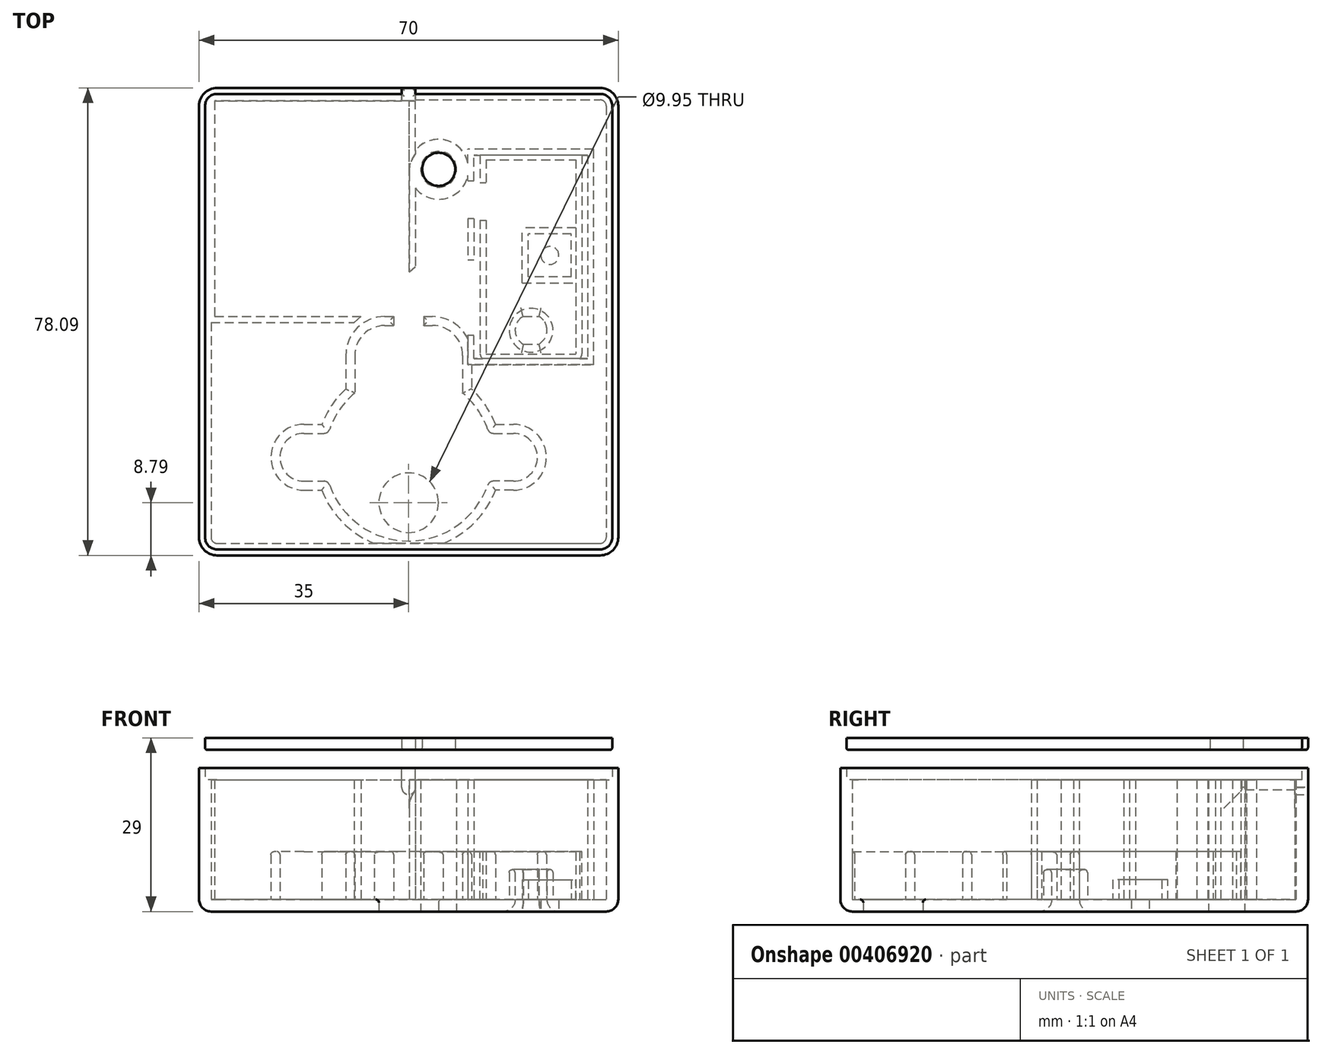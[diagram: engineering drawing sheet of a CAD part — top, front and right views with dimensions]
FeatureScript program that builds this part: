
annotation { "Feature Type Name" : "Feature", "Feature Type Description" : "" }
export const myFeature = defineFeature(function(context is Context, id is Id, definition is map)
    precondition{}
    {
        {
            var Q0;
            Q0=qCreatedBy(makeId("Top.planeOp"),FACE);
            var sketch = newSketch(context, id + "F0", { "sketchPlane" : qUnion([Q0])});
            skCircle(sketch, "E0", {"center": v(0, 0) * mm, "radius": 4.97 * mm});
            skArc(sketch, "E1", {"start": v(-13.2, 2.93) * mm, "mid": v(0, -6.4) * mm, "end": v(13.2, 2.93) * mm});
            skArc(sketch, "E2.trimOffspring", {"start": v(13.2, 12.27) * mm, "mid": v(11.5, 15.58) * mm, "end": v(9, 18.32) * mm});
            skLineSegment(sketch, "E3", {"start": v(-9, 24.6) * mm, "end": v(-9, 18.32) * mm});
            skLineSegment(sketch, "E4.MirrorCS", {"start": v(9, 24.6) * mm, "end": v(9, 18.32) * mm});
            skLineSegment(sketch, "E5", {"start": v(-4, 29.6) * mm, "end": v(4, 29.6) * mm});
            skArc(sketch, "E6.filletArc", {"start": v(-4, 29.6) * mm, "mid": v(-7.54, 28.14) * mm, "end": v(-9, 24.6) * mm});
            skArc(sketch, "E7.filletArc", {"start": v(9, 24.6) * mm, "mid": v(7.54, 28.14) * mm, "end": v(4, 29.6) * mm});
            skArc(sketch, "E8.trimOffspring", {"start": v(-9, 18.32) * mm, "mid": v(-11.5, 15.58) * mm, "end": v(-13.2, 12.27) * mm});
            skLineSegment(sketch, "E9", {"start": v(-17.5, 11.6) * mm, "end": v(-14.14, 11.6) * mm});
            skLineSegment(sketch, "E10", {"start": v(-17.5, 3.6) * mm, "end": v(-14.14, 3.6) * mm});
            skLineSegment(sketch, "E11", {"start": v(21.5, 7.6) * mm, "end": v(21.5, 7.6) * mm});
            skArc(sketch, "E12.filletArc", {"start": v(21.5, 7.6) * mm, "mid": v(20.33, 10.43) * mm, "end": v(17.5, 11.6) * mm});
            skArc(sketch, "E13.filletArc", {"start": v(17.5, 3.6) * mm, "mid": v(20.33, 4.77) * mm, "end": v(21.5, 7.6) * mm});
            skArc(sketch, "E14.MirrorCS", {"start": v(-21.5, 7.6) * mm, "mid": v(-20.33, 10.43) * mm, "end": v(-17.5, 11.6) * mm});
            skLineSegment(sketch, "E15.MirrorCS", {"start": v(-21.5, 7.6) * mm, "end": v(-21.5, 7.6) * mm});
            skArc(sketch, "E16.MirrorCS", {"start": v(-17.5, 3.6) * mm, "mid": v(-20.33, 4.77) * mm, "end": v(-21.5, 7.6) * mm});
            skLineSegment(sketch, "E17.trimOffspring", {"start": v(14.14, 11.6) * mm, "end": v(17.5, 11.6) * mm});
            skArc(sketch, "E18.filletArc", {"start": v(-14.14, 11.6) * mm, "mid": v(-13.56, 11.78) * mm, "end": v(-13.2, 12.27) * mm});
            skArc(sketch, "E19.filletArc", {"start": v(-13.2, 2.93) * mm, "mid": v(-13.56, 3.42) * mm, "end": v(-14.14, 3.6) * mm});
            skLineSegment(sketch, "E20.MirrorCS", {"start": v(17.5, 3.6) * mm, "end": v(14.14, 3.6) * mm});
            skArc(sketch, "E21.MirrorCS", {"start": v(13.2, 2.93) * mm, "mid": v(13.56, 3.42) * mm, "end": v(14.14, 3.6) * mm});
            skArc(sketch, "E22.0", {"start": v(-4, 31.1) * mm, "mid": v(-8.6, 29.2) * mm, "end": v(-10.5, 24.6) * mm});
            skLineSegment(sketch, "E22.1", {"start": v(-10.5, 24.6) * mm, "end": v(-10.5, 19) * mm});
            skArc(sketch, "E22.2", {"start": v(-10.5, 19) * mm, "mid": v(-12.84, 16.28) * mm, "end": v(-14.5, 13.1) * mm});
            skLineSegment(sketch, "E22.3", {"start": v(-17.5, 13.1) * mm, "end": v(-14.5, 13.1) * mm});
            skArc(sketch, "E22.4", {"start": v(-23, 7.6) * mm, "mid": v(-21.39, 11.49) * mm, "end": v(-17.5, 13.1) * mm});
            skLineSegment(sketch, "E22.5", {"start": v(14.5, 13.1) * mm, "end": v(17.5, 13.1) * mm});
            skArc(sketch, "E22.6", {"start": v(14.5, 13.1) * mm, "mid": v(12.84, 16.28) * mm, "end": v(10.5, 19) * mm});
            skLineSegment(sketch, "E22.7", {"start": v(10.5, 24.6) * mm, "end": v(10.5, 19) * mm});
            skArc(sketch, "E22.8", {"start": v(10.5, 24.6) * mm, "mid": v(8.6, 29.2) * mm, "end": v(4, 31.1) * mm});
            skArc(sketch, "E22.9", {"start": v(23, 7.6) * mm, "mid": v(21.39, 11.49) * mm, "end": v(17.5, 13.1) * mm});
            skArc(sketch, "E22.10", {"start": v(17.5, 2.1) * mm, "mid": v(21.39, 3.71) * mm, "end": v(23, 7.6) * mm});
            skLineSegment(sketch, "E22.11", {"start": v(17.5, 2.1) * mm, "end": v(14.5, 2.1) * mm});
            skArc(sketch, "E22.12", {"start": v(-14.5, 2.1) * mm, "mid": v(0, -7.9) * mm, "end": v(14.5, 2.1) * mm});
            skLineSegment(sketch, "E22.13", {"start": v(-17.5, 2.1) * mm, "end": v(-14.5, 2.1) * mm});
            skLineSegment(sketch, "E22.14", {"start": v(-4, 31.1) * mm, "end": v(4, 31.1) * mm});
            skArc(sketch, "E22.15", {"start": v(-17.5, 2.1) * mm, "mid": v(-21.39, 3.71) * mm, "end": v(-23, 7.6) * mm});
            skPoint(sketch, "E23.visualSharp", {"position": v(13.42, 11.6) * mm});
            skArc(sketch, "E23.filletArc", {"start": v(13.2, 12.27) * mm, "mid": v(13.56, 11.78) * mm, "end": v(14.14, 11.6) * mm});
            skLineSegment(sketch, "E24", {"start": v(-2.49, 31.1) * mm, "end": v(-2.49, 29.6) * mm});
            skLineSegment(sketch, "E25.MirrorCS", {"start": v(2.49, 31.1) * mm, "end": v(2.49, 29.6) * mm});
            skSolve(sketch);
        }
        {
            var Q0;
            Q0=makeQuery(id+"F0.imprint","IMPRINT",FACE,{"disambiguationData":[TD([[makeQuery(id+"F0.imprint","IMPRINT",EDGE,{"derivedFrom":sQuery(id+"F0.wireOp",EDGE,"E0")}),-1.0]])]});
            extrude(context, id + "F1", {"entities" : qUnion([Q0]), "depth" : 1.5 * mm, "offsetDistance" : 25 * mm});
        }
        {
            var Q0;
            Q0=makeQuery(id+"F0.imprint","IMPRINT",FACE,{"disambiguationData":[TD([[makeQuery(id+"F0.imprint","IMPRINT",EDGE,{"derivedFrom":sQuery(id+"F0.wireOp",EDGE,"E1")}),-1.0]])]});
            extrude(context, id + "F2", {"entities" : qUnion([Q0]), "operationType" : NewBodyOperationType.ADD, "depth" : 10 * mm});
        }
        {
            var Q0;
            Q0=qCreatedBy(makeId("Top.planeOp"),FACE);
            var sketch = newSketch(context, id + "F3", { "sketchPlane" : qUnion([Q0])});
            skLineSegment(sketch, "E26.bottom", {"start": v(-32, 67.3) * mm, "end": v(32, 67.3) * mm});
            skLineSegment(sketch, "E26.top", {"start": v(-32, -6.79) * mm, "end": v(32, -6.79) * mm});
            skLineSegment(sketch, "E26.left", {"start": v(-33, 66.3) * mm, "end": v(-33, -5.79) * mm});
            skLineSegment(sketch, "E26.right", {"start": v(33, 66.3) * mm, "end": v(33, -5.79) * mm});
            skPoint(sketch, "E27.visualSharp", {"position": v(-33, 67.3) * mm});
            skArc(sketch, "E27.filletArc", {"start": v(-32, 67.3) * mm, "mid": v(-32.7, 67) * mm, "end": v(-33, 66.3) * mm});
            skPoint(sketch, "E28.visualSharp", {"position": v(33, 67.3) * mm});
            skArc(sketch, "E28.filletArc", {"start": v(33, 66.3) * mm, "mid": v(32.7, 67) * mm, "end": v(32, 67.3) * mm});
            skPoint(sketch, "E29.visualSharp", {"position": v(-33, -6.79) * mm});
            skArc(sketch, "E29.filletArc", {"start": v(-33, -5.79) * mm, "mid": v(-32.7, -6.5) * mm, "end": v(-32, -6.79) * mm});
            skPoint(sketch, "E30.visualSharp", {"position": v(33, -6.79) * mm});
            skArc(sketch, "E30.filletArc", {"start": v(32, -6.79) * mm, "mid": v(32.7, -6.5) * mm, "end": v(33, -5.79) * mm});
            skArc(sketch, "E31.0", {"start": v(34, 66.3) * mm, "mid": v(33.41, 67.71) * mm, "end": v(32, 68.3) * mm});
            skLineSegment(sketch, "E31.1", {"start": v(-32, 68.3) * mm, "end": v(32, 68.3) * mm});
            skLineSegment(sketch, "E31.2", {"start": v(34, 66.3) * mm, "end": v(34, -5.79) * mm});
            skArc(sketch, "E31.3", {"start": v(-32, 68.3) * mm, "mid": v(-33.41, 67.71) * mm, "end": v(-34, 66.3) * mm});
            skArc(sketch, "E31.4", {"start": v(32, -7.79) * mm, "mid": v(33.41, -7.2) * mm, "end": v(34, -5.79) * mm});
            skLineSegment(sketch, "E31.5", {"start": v(-32, -7.79) * mm, "end": v(32, -7.79) * mm});
            skArc(sketch, "E31.6", {"start": v(-34, -5.79) * mm, "mid": v(-33.41, -7.2) * mm, "end": v(-32, -7.79) * mm});
            skLineSegment(sketch, "E31.7", {"start": v(-34, 66.3) * mm, "end": v(-34, -5.79) * mm});
            skArc(sketch, "E32.0", {"start": v(35, 66.3) * mm, "mid": v(34.12, 68.42) * mm, "end": v(32, 69.3) * mm});
            skLineSegment(sketch, "E32.1", {"start": v(-32, 69.3) * mm, "end": v(32, 69.3) * mm});
            skLineSegment(sketch, "E32.2", {"start": v(35, 66.3) * mm, "end": v(35, -5.79) * mm});
            skArc(sketch, "E32.3", {"start": v(-32, 69.3) * mm, "mid": v(-34.12, 68.42) * mm, "end": v(-35, 66.3) * mm});
            skArc(sketch, "E32.4", {"start": v(32, -8.79) * mm, "mid": v(34.12, -7.9) * mm, "end": v(35, -5.79) * mm});
            skLineSegment(sketch, "E32.5", {"start": v(-32, -8.79) * mm, "end": v(32, -8.79) * mm});
            skArc(sketch, "E32.6", {"start": v(-35, -5.79) * mm, "mid": v(-34.12, -7.9) * mm, "end": v(-32, -8.79) * mm});
            skLineSegment(sketch, "E32.7", {"start": v(-35, 66.3) * mm, "end": v(-35, -5.79) * mm});
            skSolve(sketch);
        }
        {
            var Q0;
            Q0=makeQuery(id+"F3.imprint","IMPRINT",FACE,{"disambiguationData":[TD([[makeQuery(id+"F3.imprint","IMPRINT",EDGE,{"derivedFrom":sQuery(id+"F3.wireOp",EDGE,"E26.bottom")}),-1.0]])]});
            extrude(context, id + "F4", {"entities" : qUnion([Q0]), "operationType" : NewBodyOperationType.ADD, "depth" : 2 * mm, "offsetDistance" : 25 * mm});
        }
        {
            var Q0;
            Q0=makeQuery(id+"F0.imprint","IMPRINT",FACE,{"disambiguationData":[TD([[makeQuery(id+"F0.imprint","IMPRINT",EDGE,{"derivedFrom":sQuery(id+"F0.wireOp",EDGE,"E0")}),1.0]])]});
            extrude(context, id + "F5", {"entities" : qUnion([Q0]), "operationType" : NewBodyOperationType.REMOVE, "depth" : 25 * mm, "offsetDistance" : 25 * mm});
        }
        {
            var Q0;
            {var subQ0=sQuery(id+"F3.wireOp",EDGE,"E26.bottom");var subQ1=sQuery(id+"F3.wireOp",EDGE,"E26.top");var subQ2=sQuery(id+"F3.wireOp",EDGE,"E26.left");var subQ3=sQuery(id+"F3.wireOp",EDGE,"E26.right");Q0=makeQuery(id+"F4.boolean.opBoolean","SPLIT",FACE,{"disambiguationData":[TD([makeQuery(id+"F2.opExtrude","SWEPT_FACE",FACE,{"disambiguationData":[OSD([sQuery(id+"F0.wireOp",EDGE,"E22.0")])]})])],"derivedFrom":makeQuery(id+"F4.opExtrude","CAP_FACE",FACE,{"disambiguationData":[OSD([subQ0,subQ1,subQ2,subQ3])],"isStart":false})});}
            var sketch = newSketch(context, id + "F6", { "sketchPlane" : qUnion([Q0])});
            skArc(sketch, "E33", {"start": v(19.1, 31.12) * mm, "mid": v(17.78, 28.79) * mm, "end": v(19.16, 26.49) * mm});
            skCircle(sketch, "E34.0", {"center": v(20.44, 28.82) * mm, "radius": 3.66 * mm});
            skLineSegment(sketch, "E35.0", {"start": v(19.16, 26.49) * mm, "end": v(21.72, 26.49) * mm});
            skLineSegment(sketch, "E36.MirrorCS", {"start": v(19.1, 31.12) * mm, "end": v(21.78, 31.12) * mm});
            skArc(sketch, "E37.trimOffspring", {"start": v(21.72, 26.49) * mm, "mid": v(23.1, 28.79) * mm, "end": v(21.78, 31.12) * mm});
            skPoint(sketch, "E38.orphan", {"position": v(22.74, 31.48) * mm});
            skPoint(sketch, "E39.orphan", {"position": v(22.74, 26.54) * mm});
            skPoint(sketch, "E40.orphan", {"position": v(18.11, 26.54) * mm});
            skPoint(sketch, "E41.orphan", {"position": v(18.11, 31.48) * mm});
            skLineSegment(sketch, "E42", {"start": v(20.44, 28.82) * mm, "end": v(20.44, 32.48) * mm, "construction": true});
            skLineSegment(sketch, "E43", {"start": v(27.94, 41.32) * mm, "end": v(36.64, 41.32) * mm, "construction": true});
            skLineSegment(sketch, "E44", {"start": v(27.94, 57.32) * mm, "end": v(27.94, 24.92) * mm});
            skLineSegment(sketch, "E45", {"start": v(12.94, 57.32) * mm, "end": v(27.94, 57.32) * mm});
            skLineSegment(sketch, "E46", {"start": v(13.04, 24.82) * mm, "end": v(27.84, 24.82) * mm});
            skArc(sketch, "E47.filletArc", {"start": v(27.84, 24.82) * mm, "mid": v(27.91, 24.85) * mm, "end": v(27.94, 24.92) * mm});
            skLineSegment(sketch, "E48.MirrorCS", {"start": v(12.94, 57.32) * mm, "end": v(12.94, 53.45) * mm});
            skPoint(sketch, "E49.newPointB", {"position": v(12.94, 24.92) * mm});
            skArc(sketch, "E49.filletArc", {"start": v(12.94, 24.92) * mm, "mid": v(12.97, 24.85) * mm, "end": v(13.04, 24.82) * mm});
            skArc(sketch, "E50.0", {"start": v(11.94, 24.92) * mm, "mid": v(12.26, 24.14) * mm, "end": v(13.04, 23.82) * mm});
            skArc(sketch, "E50.1", {"start": v(27.84, 23.82) * mm, "mid": v(28.62, 24.14) * mm, "end": v(28.94, 24.92) * mm});
            skLineSegment(sketch, "E50.2", {"start": v(28.94, 58.32) * mm, "end": v(28.94, 24.92) * mm});
            skLineSegment(sketch, "E50.3", {"start": v(13.04, 23.82) * mm, "end": v(27.84, 23.82) * mm});
            skLineSegment(sketch, "E50.4", {"start": v(11.94, 58.32) * mm, "end": v(28.94, 58.32) * mm});
            skLineSegment(sketch, "E50.5", {"start": v(11.94, 58.32) * mm, "end": v(11.94, 53.45) * mm});
            skLineSegment(sketch, "E51", {"start": v(11.94, 53.45) * mm, "end": v(12.94, 53.45) * mm});
            skLineSegment(sketch, "E52", {"start": v(11.94, 47.2) * mm, "end": v(12.94, 47.2) * mm});
            skLineSegment(sketch, "E53.trimOffspring", {"start": v(12.94, 47.2) * mm, "end": v(12.94, 24.92) * mm});
            skLineSegment(sketch, "E54.trimOffspring", {"start": v(11.94, 47.2) * mm, "end": v(11.94, 24.92) * mm});
            skSolve(sketch);
        }
        {
            var Q0;
            Q0=makeQuery(id+"F6.imprint","IMPRINT",FACE,{"disambiguationData":[TD([[makeQuery(id+"F6.imprint","IMPRINT",EDGE,{"derivedFrom":sQuery(id+"F6.wireOp",EDGE,"E33")}),-1.0]])]});
            extrude(context, id + "F7", {"entities" : qUnion([Q0]), "operationType" : NewBodyOperationType.ADD, "depth" : 5 * mm, "offsetDistance" : 25 * mm});
        }
        {
            var Q0;
            {var subQ0=sQuery(id+"F3.wireOp",EDGE,"E26.bottom");var subQ1=sQuery(id+"F3.wireOp",EDGE,"E26.top");var subQ2=sQuery(id+"F3.wireOp",EDGE,"E26.left");var subQ3=sQuery(id+"F3.wireOp",EDGE,"E26.right");Q0=makeQuery(id+"F7.boolean.opBoolean","SPLIT",FACE,{"disambiguationData":[TD([makeQuery(id+"F7.opExtrude","SWEPT_FACE",FACE,{"disambiguationData":[OSD([sQuery(id+"F6.wireOp",EDGE,"E33")])]})])],"derivedFrom":makeQuery(id+"F4.boolean.opBoolean","SPLIT",FACE,{"disambiguationData":[TD([makeQuery(id+"F2.opExtrude","SWEPT_FACE",FACE,{"disambiguationData":[OSD([sQuery(id+"F0.wireOp",EDGE,"E22.0")])]})])],"derivedFrom":makeQuery(id+"F4.opExtrude","CAP_FACE",FACE,{"disambiguationData":[OSD([subQ0,subQ1,subQ2,subQ3])],"isStart":false})})});}
            extrude(context, id + "F8", {"entities" : qUnion([Q0]), "operationType" : NewBodyOperationType.REMOVE, "oppositeDirection" : true, "depth" : 25 * mm, "offsetDistance" : 25 * mm});
        }
        {
            var Q0;
            Q0=makeQuery(id+"F2.opExtrude","CAP_FACE",FACE,{"disambiguationData":[OSD([sQuery(id+"F0.wireOp",EDGE,"E1"),sQuery(id+"F0.wireOp",EDGE,"E2.trimOffspring"),sQuery(id+"F0.wireOp",EDGE,"E3"),sQuery(id+"F0.wireOp",EDGE,"E4.MirrorCS"),sQuery(id+"F0.wireOp",EDGE,"E5"),sQuery(id+"F0.wireOp",EDGE,"E6.filletArc"),sQuery(id+"F0.wireOp",EDGE,"E7.filletArc"),sQuery(id+"F0.wireOp",EDGE,"E8.trimOffspring"),sQuery(id+"F0.wireOp",EDGE,"E9"),sQuery(id+"F0.wireOp",EDGE,"E10"),sQuery(id+"F0.wireOp",EDGE,"E12.filletArc"),sQuery(id+"F0.wireOp",EDGE,"E13.filletArc"),sQuery(id+"F0.wireOp",EDGE,"E14.MirrorCS"),sQuery(id+"F0.wireOp",EDGE,"E16.MirrorCS"),sQuery(id+"F0.wireOp",EDGE,"E17.trimOffspring"),sQuery(id+"F0.wireOp",EDGE,"E18.filletArc"),sQuery(id+"F0.wireOp",EDGE,"E19.filletArc"),sQuery(id+"F0.wireOp",EDGE,"E20.MirrorCS"),sQuery(id+"F0.wireOp",EDGE,"E21.MirrorCS"),sQuery(id+"F0.wireOp",EDGE,"E22.0"),sQuery(id+"F0.wireOp",EDGE,"E22.1"),sQuery(id+"F0.wireOp",EDGE,"E22.2"),sQuery(id+"F0.wireOp",EDGE,"E22.3"),sQuery(id+"F0.wireOp",EDGE,"E22.4"),sQuery(id+"F0.wireOp",EDGE,"E22.5"),sQuery(id+"F0.wireOp",EDGE,"E22.6"),sQuery(id+"F0.wireOp",EDGE,"E22.7"),sQuery(id+"F0.wireOp",EDGE,"E22.8"),sQuery(id+"F0.wireOp",EDGE,"E22.9"),sQuery(id+"F0.wireOp",EDGE,"E22.10"),sQuery(id+"F0.wireOp",EDGE,"E22.11"),sQuery(id+"F0.wireOp",EDGE,"E22.12"),sQuery(id+"F0.wireOp",EDGE,"E22.13"),sQuery(id+"F0.wireOp",EDGE,"E22.14"),sQuery(id+"F0.wireOp",EDGE,"E22.15"),sQuery(id+"F0.wireOp",EDGE,"E23.filletArc")])],"isStart":false});
            var Q1;
            Q1=makeQuery(id+"F7.opExtrude","CAP_FACE",FACE,{"disambiguationData":[OSD([sQuery(id+"F6.wireOp",EDGE,"E33"),sQuery(id+"F6.wireOp",EDGE,"E34.0")])],"isStart":false});
            var Q2;
            Q2=makeQuery(id+"F5.boolean.opBoolean","INTERSECT",EDGE,{"derivedFrom":[makeQuery(id+"F4.boolean.opBoolean","SPLIT",FACE,{"disambiguationData":[TD([makeQuery(id+"F2.opExtrude","SWEPT_FACE",FACE,{"disambiguationData":[OSD([sQuery(id+"F0.wireOp",EDGE,"E1")])]})])],"derivedFrom":makeQuery(id+"F4.opExtrude","CAP_FACE",FACE,{"disambiguationData":[OSD([sQuery(id+"F3.wireOp",EDGE,"E26.bottom"),sQuery(id+"F3.wireOp",EDGE,"E26.top"),sQuery(id+"F3.wireOp",EDGE,"E26.left"),sQuery(id+"F3.wireOp",EDGE,"E26.right")])],"isStart":false})}),makeQuery(id+"F5.opExtrude","SWEPT_FACE",FACE,{"disambiguationData":[OSD([sQuery(id+"F0.wireOp",EDGE,"E0")])]})]});
            fillet(context, id + "F9", {"entities" : qUnion([Q0, Q1, Q2]), "radius" : 0.5 * mm, "tangentPropagation" : true, "allowEdgeOverflow" : false});
        }
        {
            var Q0;
            Q0=qCreatedBy(makeId("Top.planeOp"),FACE);
            var sketch = newSketch(context, id + "F10", { "sketchPlane" : qUnion([Q0])});
            skLineSegment(sketch, "E55.bottom", {"start": v(29.9, 24.07) * mm, "end": v(10.9, 24.07) * mm});
            skLineSegment(sketch, "E55.top", {"start": v(29.9, 58.07) * mm, "end": v(10.9, 58.07) * mm});
            skLineSegment(sketch, "E55.left", {"start": v(29.9, 24.07) * mm, "end": v(29.9, 58.07) * mm});
            skLineSegment(sketch, "E55.right", {"start": v(10.9, 24.07) * mm, "end": v(10.9, 28.04) * mm});
            skLineSegment(sketch, "E56.0", {"start": v(30.9, 59.07) * mm, "end": v(9.9, 59.07) * mm});
            skLineSegment(sketch, "E56.1", {"start": v(30.9, 23.07) * mm, "end": v(30.9, 59.07) * mm});
            skLineSegment(sketch, "E56.2", {"start": v(30.9, 23.07) * mm, "end": v(9.9, 23.07) * mm});
            skLineSegment(sketch, "E56.3", {"start": v(9.9, 23.07) * mm, "end": v(9.9, 28.04) * mm});
            skLineSegment(sketch, "E57", {"start": v(9.9, 40.53) * mm, "end": v(10.9, 40.53) * mm});
            skLineSegment(sketch, "E58", {"start": v(9.9, 28.04) * mm, "end": v(10.9, 28.04) * mm});
            skLineSegment(sketch, "E59.trimOffspring", {"start": v(9.9, 40.53) * mm, "end": v(9.9, 47.44) * mm});
            skLineSegment(sketch, "E60.trimOffspring", {"start": v(10.9, 40.53) * mm, "end": v(10.9, 47.44) * mm});
            skLineSegment(sketch, "E61", {"start": v(9.9, 53.82) * mm, "end": v(10.9, 53.82) * mm});
            skLineSegment(sketch, "E62", {"start": v(9.9, 47.44) * mm, "end": v(10.9, 47.44) * mm});
            skLineSegment(sketch, "E63.trimOffspring", {"start": v(9.9, 53.82) * mm, "end": v(9.9, 59.07) * mm});
            skLineSegment(sketch, "E64.trimOffspring", {"start": v(10.9, 53.82) * mm, "end": v(10.9, 58.07) * mm});
            skSolve(sketch);
        }
        {
            var Q0;
            Q0=qCreatedBy(makeId("Top.planeOp"),FACE);
            var sketch = newSketch(context, id + "F11", { "sketchPlane" : qUnion([Q0])});
            skLineSegment(sketch, "E65.bottom", {"start": v(-32.41, 67.13) * mm, "end": v(0.09, 67.13) * mm});
            skLineSegment(sketch, "E65.top", {"start": v(-32.41, 31.13) * mm, "end": v(-8, 31.13) * mm});
            skLineSegment(sketch, "E65.left", {"start": v(-32.41, 67.13) * mm, "end": v(-32.41, 31.13) * mm});
            skLineSegment(sketch, "E65.right", {"start": v(0.09, 67.13) * mm, "end": v(0.09, 38.55) * mm});
            skLineSegment(sketch, "E66", {"start": v(5, 57.94) * mm, "end": v(5, 42.38) * mm});
            skCircle(sketch, "E67", {"center": v(5, 55.7) * mm, "radius": 3 * mm});
            skLineSegment(sketch, "E68.0", {"start": v(-33.41, 30.13) * mm, "end": v(-9.08, 30.13) * mm});
            skLineSegment(sketch, "E68.1", {"start": v(-33.41, 68.13) * mm, "end": v(-33.41, 30.13) * mm});
            skLineSegment(sketch, "E68.2", {"start": v(-33.41, 68.13) * mm, "end": v(1.09, 68.13) * mm});
            skLineSegment(sketch, "E68.3", {"start": v(1.09, 68.13) * mm, "end": v(1.09, 39.47) * mm});
            skLineSegment(sketch, "E69", {"start": v(-9.08, 30.13) * mm, "end": v(-8, 31.13) * mm});
            skLineSegment(sketch, "E70.trimOffspring", {"start": v(0.09, 38.55) * mm, "end": v(1.09, 39.47) * mm});
            skArc(sketch, "E71.trimOffspring", {"start": v(1.09, 52.59) * mm, "mid": v(10, 55.7) * mm, "end": v(1.09, 58.82) * mm});
            skSolve(sketch);
        }
        {
            var Q0;
            Q0=makeQuery(id+"F10.imprint","IMPRINT",FACE,{"disambiguationData":[TD([[makeQuery(id+"F10.imprint","IMPRINT",EDGE,{"derivedFrom":sQuery(id+"F10.wireOp",EDGE,"E55.bottom")}),1.0]])]});
            var Q1;
            Q1=makeQuery(id+"F10.imprint","IMPRINT",FACE,{"disambiguationData":[TD([[makeQuery(id+"F10.imprint","IMPRINT",EDGE,{"derivedFrom":sQuery(id+"F10.wireOp",EDGE,"E57")}),1.0]])]});
            extrude(context, id + "F12", {"entities" : qUnion([Q0, Q1]), "operationType" : NewBodyOperationType.ADD, "depth" : 22 * mm, "offsetDistance" : 25 * mm});
        }
        {
            var Q0;
            Q0=makeQuery(id+"F11.imprint","IMPRINT",FACE,{"disambiguationData":[TD([[makeQuery(id+"F11.imprint","IMPRINT",EDGE,{"derivedFrom":sQuery(id+"F11.wireOp",EDGE,"E67")}),1.0]])]});
            extrude(context, id + "F13", {"entities" : qUnion([Q0]), "operationType" : NewBodyOperationType.REMOVE, "depth" : 25 * mm, "offsetDistance" : 25 * mm});
        }
        {
            var Q0;
            Q0=makeQuery(id+"F11.imprint","IMPRINT",FACE,{"disambiguationData":[TD([[makeQuery(id+"F11.imprint","IMPRINT",EDGE,{"derivedFrom":sQuery(id+"F11.wireOp",EDGE,"E67")}),-1.0]])]});
            extrude(context, id + "F14", {"entities" : qUnion([Q0]), "operationType" : NewBodyOperationType.ADD, "depth" : 22 * mm, "offsetDistance" : 25 * mm});
        }
        {
            var Q0;
            Q0=makeQuery(id+"F11.imprint","IMPRINT",FACE,{"disambiguationData":[TD([[makeQuery(id+"F11.imprint","IMPRINT",EDGE,{"derivedFrom":sQuery(id+"F11.wireOp",EDGE,"E65.bottom")}),1.0]])]});
            extrude(context, id + "F15", {"entities" : qUnion([Q0]), "operationType" : NewBodyOperationType.ADD, "depth" : 22 * mm, "offsetDistance" : 25 * mm});
        }
        {
            var Q0;
            Q0=makeQuery(id+"F3.imprint","IMPRINT",FACE,{"disambiguationData":[TD([[makeQuery(id+"F3.imprint","IMPRINT",EDGE,{"derivedFrom":sQuery(id+"F3.wireOp",EDGE,"E26.bottom")}),1.0]])]});
            extrude(context, id + "F16", {"entities" : qUnion([Q0]), "operationType" : NewBodyOperationType.ADD, "depth" : 22 * mm, "offsetDistance" : 25 * mm});
        }
        {
            var Q0;
            Q0 = qSketchRegion(id + "F3", true);
            extrude(context, id + "F17", {"entities" : qUnion([Q0]), "operationType" : NewBodyOperationType.ADD, "depth" : 24 * mm, "offsetDistance" : 25 * mm});
        }
        {
            var Q0;
            Q0=makeQuery(id+"F17.opExtrude","CAP_EDGE",EDGE,{"disambiguationData":[OSD([sQuery(id+"F3.wireOp",EDGE,"E32.2")])],"isStart":true});
            var Q1;
            Q1=makeQuery(id+"F17.opExtrude","CAP_EDGE",EDGE,{"disambiguationData":[OSD([sQuery(id+"F3.wireOp",EDGE,"E32.5")])],"isStart":true});
            var Q2;
            Q2=makeQuery(id+"F17.opExtrude","CAP_EDGE",EDGE,{"disambiguationData":[OSD([sQuery(id+"F3.wireOp",EDGE,"E32.4")])],"isStart":true});
            var Q3;
            Q3=makeQuery(id+"F17.opExtrude","CAP_EDGE",EDGE,{"disambiguationData":[OSD([sQuery(id+"F3.wireOp",EDGE,"E32.6")])],"isStart":true});
            var Q4;
            Q4=makeQuery(id+"F17.opExtrude","CAP_EDGE",EDGE,{"disambiguationData":[OSD([sQuery(id+"F3.wireOp",EDGE,"E32.7")])],"isStart":true});
            var Q5;
            Q5=makeQuery(id+"F17.opExtrude","CAP_EDGE",EDGE,{"disambiguationData":[OSD([sQuery(id+"F3.wireOp",EDGE,"E32.3")])],"isStart":true});
            var Q6;
            Q6=makeQuery(id+"F17.opExtrude","CAP_EDGE",EDGE,{"disambiguationData":[OSD([sQuery(id+"F3.wireOp",EDGE,"E32.1")])],"isStart":true});
            var Q7;
            Q7=makeQuery(id+"F17.opExtrude","CAP_EDGE",EDGE,{"disambiguationData":[OSD([sQuery(id+"F3.wireOp",EDGE,"E32.0")])],"isStart":true});
            var Q8;
            {var subQ0=sQuery(id+"F0.wireOp",EDGE,"E23.filletArc");var subQ1=sQuery(id+"F0.wireOp",EDGE,"E21.MirrorCS");var subQ2=sQuery(id+"F0.wireOp",EDGE,"E20.MirrorCS");var subQ3=sQuery(id+"F0.wireOp",EDGE,"E19.filletArc");var subQ4=sQuery(id+"F0.wireOp",EDGE,"E18.filletArc");var subQ5=sQuery(id+"F0.wireOp",EDGE,"E17.trimOffspring");var subQ6=sQuery(id+"F0.wireOp",EDGE,"E16.MirrorCS");var subQ7=sQuery(id+"F0.wireOp",EDGE,"E14.MirrorCS");var subQ8=sQuery(id+"F0.wireOp",EDGE,"E13.filletArc");var subQ9=sQuery(id+"F0.wireOp",EDGE,"E12.filletArc");var subQ10=sQuery(id+"F0.wireOp",EDGE,"E10");var subQ11=sQuery(id+"F0.wireOp",EDGE,"E9");var subQ12=sQuery(id+"F0.wireOp",EDGE,"E8.trimOffspring");var subQ13=sQuery(id+"F0.wireOp",EDGE,"E7.filletArc");var subQ14=sQuery(id+"F0.wireOp",EDGE,"E6.filletArc");var subQ15=sQuery(id+"F0.wireOp",EDGE,"E5");var subQ16=sQuery(id+"F0.wireOp",EDGE,"E4.MirrorCS");var subQ17=sQuery(id+"F0.wireOp",EDGE,"E3");var subQ18=sQuery(id+"F0.wireOp",EDGE,"E2.trimOffspring");var subQ19=sQuery(id+"F0.wireOp",EDGE,"E1");Q8=makeQuery(id+"F8.boolean.opBoolean","INTERSECT",EDGE,{"derivedFrom":[makeQuery(id+"F4.boolean.opBoolean","MERGE",FACE,{"derivedFrom":[makeQuery(id+"F2.boolean.opBoolean","MERGE",FACE,{"derivedFrom":[makeQuery(id+"F1.opExtrude","CAP_FACE",FACE,{"disambiguationData":[OSD([sQuery(id+"F0.wireOp",EDGE,"E0"),subQ19,subQ18,subQ17,subQ16,subQ15,subQ14,subQ13,subQ12,subQ11,subQ10,subQ9,subQ8,subQ7,subQ6,subQ5,subQ4,subQ3,subQ2,subQ1,subQ0])],"isStart":true}),makeQuery(id+"F2.opExtrude","CAP_FACE",FACE,{"disambiguationData":[OSD([subQ19,subQ18,subQ17,subQ16,subQ15,subQ14,subQ13,subQ12,subQ11,subQ10,subQ9,subQ8,subQ7,subQ6,subQ5,subQ4,subQ3,subQ2,subQ1,sQuery(id+"F0.wireOp",EDGE,"E22.0"),sQuery(id+"F0.wireOp",EDGE,"E22.1"),sQuery(id+"F0.wireOp",EDGE,"E22.2"),sQuery(id+"F0.wireOp",EDGE,"E22.3"),sQuery(id+"F0.wireOp",EDGE,"E22.4"),sQuery(id+"F0.wireOp",EDGE,"E22.5"),sQuery(id+"F0.wireOp",EDGE,"E22.6"),sQuery(id+"F0.wireOp",EDGE,"E22.7"),sQuery(id+"F0.wireOp",EDGE,"E22.8"),sQuery(id+"F0.wireOp",EDGE,"E22.9"),sQuery(id+"F0.wireOp",EDGE,"E22.10"),sQuery(id+"F0.wireOp",EDGE,"E22.11"),sQuery(id+"F0.wireOp",EDGE,"E22.12"),sQuery(id+"F0.wireOp",EDGE,"E22.13"),sQuery(id+"F0.wireOp",EDGE,"E22.14"),sQuery(id+"F0.wireOp",EDGE,"E22.15"),subQ0,sQuery(id+"F0.wireOp",EDGE,"E24"),sQuery(id+"F0.wireOp",EDGE,"E25.MirrorCS")])],"isStart":true})]}),makeQuery(id+"F4.opExtrude","CAP_FACE",FACE,{"disambiguationData":[OSD([sQuery(id+"F3.wireOp",EDGE,"E26.bottom"),sQuery(id+"F3.wireOp",EDGE,"E26.top"),sQuery(id+"F3.wireOp",EDGE,"E26.left"),sQuery(id+"F3.wireOp",EDGE,"E26.right"),sQuery(id+"F3.wireOp",EDGE,"E27.filletArc"),sQuery(id+"F3.wireOp",EDGE,"E28.filletArc"),sQuery(id+"F3.wireOp",EDGE,"E29.filletArc"),sQuery(id+"F3.wireOp",EDGE,"E30.filletArc")])],"isStart":true})]}),makeQuery(id+"F8.opExtrude","SWEPT_FACE",FACE,{"disambiguationData":[OSD([sQuery(id+"F6.wireOp",EDGE,"E36.MirrorCS")])]})]});}
            var Q9;
            {var subQ0=sQuery(id+"F0.wireOp",EDGE,"E23.filletArc");var subQ1=sQuery(id+"F0.wireOp",EDGE,"E21.MirrorCS");var subQ2=sQuery(id+"F0.wireOp",EDGE,"E20.MirrorCS");var subQ3=sQuery(id+"F0.wireOp",EDGE,"E19.filletArc");var subQ4=sQuery(id+"F0.wireOp",EDGE,"E18.filletArc");var subQ5=sQuery(id+"F0.wireOp",EDGE,"E17.trimOffspring");var subQ6=sQuery(id+"F0.wireOp",EDGE,"E16.MirrorCS");var subQ7=sQuery(id+"F0.wireOp",EDGE,"E14.MirrorCS");var subQ8=sQuery(id+"F0.wireOp",EDGE,"E13.filletArc");var subQ9=sQuery(id+"F0.wireOp",EDGE,"E12.filletArc");var subQ10=sQuery(id+"F0.wireOp",EDGE,"E10");var subQ11=sQuery(id+"F0.wireOp",EDGE,"E9");var subQ12=sQuery(id+"F0.wireOp",EDGE,"E8.trimOffspring");var subQ13=sQuery(id+"F0.wireOp",EDGE,"E7.filletArc");var subQ14=sQuery(id+"F0.wireOp",EDGE,"E6.filletArc");var subQ15=sQuery(id+"F0.wireOp",EDGE,"E5");var subQ16=sQuery(id+"F0.wireOp",EDGE,"E4.MirrorCS");var subQ17=sQuery(id+"F0.wireOp",EDGE,"E3");var subQ18=sQuery(id+"F0.wireOp",EDGE,"E2.trimOffspring");var subQ19=sQuery(id+"F0.wireOp",EDGE,"E1");Q9=makeQuery(id+"F8.boolean.opBoolean","INTERSECT",EDGE,{"derivedFrom":[makeQuery(id+"F4.boolean.opBoolean","MERGE",FACE,{"derivedFrom":[makeQuery(id+"F2.boolean.opBoolean","MERGE",FACE,{"derivedFrom":[makeQuery(id+"F1.opExtrude","CAP_FACE",FACE,{"disambiguationData":[OSD([sQuery(id+"F0.wireOp",EDGE,"E0"),subQ19,subQ18,subQ17,subQ16,subQ15,subQ14,subQ13,subQ12,subQ11,subQ10,subQ9,subQ8,subQ7,subQ6,subQ5,subQ4,subQ3,subQ2,subQ1,subQ0])],"isStart":true}),makeQuery(id+"F2.opExtrude","CAP_FACE",FACE,{"disambiguationData":[OSD([subQ19,subQ18,subQ17,subQ16,subQ15,subQ14,subQ13,subQ12,subQ11,subQ10,subQ9,subQ8,subQ7,subQ6,subQ5,subQ4,subQ3,subQ2,subQ1,sQuery(id+"F0.wireOp",EDGE,"E22.0"),sQuery(id+"F0.wireOp",EDGE,"E22.1"),sQuery(id+"F0.wireOp",EDGE,"E22.2"),sQuery(id+"F0.wireOp",EDGE,"E22.3"),sQuery(id+"F0.wireOp",EDGE,"E22.4"),sQuery(id+"F0.wireOp",EDGE,"E22.5"),sQuery(id+"F0.wireOp",EDGE,"E22.6"),sQuery(id+"F0.wireOp",EDGE,"E22.7"),sQuery(id+"F0.wireOp",EDGE,"E22.8"),sQuery(id+"F0.wireOp",EDGE,"E22.9"),sQuery(id+"F0.wireOp",EDGE,"E22.10"),sQuery(id+"F0.wireOp",EDGE,"E22.11"),sQuery(id+"F0.wireOp",EDGE,"E22.12"),sQuery(id+"F0.wireOp",EDGE,"E22.13"),sQuery(id+"F0.wireOp",EDGE,"E22.14"),sQuery(id+"F0.wireOp",EDGE,"E22.15"),subQ0,sQuery(id+"F0.wireOp",EDGE,"E24"),sQuery(id+"F0.wireOp",EDGE,"E25.MirrorCS")])],"isStart":true})]}),makeQuery(id+"F4.opExtrude","CAP_FACE",FACE,{"disambiguationData":[OSD([sQuery(id+"F3.wireOp",EDGE,"E26.bottom"),sQuery(id+"F3.wireOp",EDGE,"E26.top"),sQuery(id+"F3.wireOp",EDGE,"E26.left"),sQuery(id+"F3.wireOp",EDGE,"E26.right"),sQuery(id+"F3.wireOp",EDGE,"E27.filletArc"),sQuery(id+"F3.wireOp",EDGE,"E28.filletArc"),sQuery(id+"F3.wireOp",EDGE,"E29.filletArc"),sQuery(id+"F3.wireOp",EDGE,"E30.filletArc")])],"isStart":true})]}),makeQuery(id+"F8.opExtrude","SWEPT_FACE",FACE,{"disambiguationData":[OSD([sQuery(id+"F6.wireOp",EDGE,"E33")])]})]});}
            var Q10;
            {var subQ0=sQuery(id+"F0.wireOp",EDGE,"E23.filletArc");var subQ1=sQuery(id+"F0.wireOp",EDGE,"E21.MirrorCS");var subQ2=sQuery(id+"F0.wireOp",EDGE,"E20.MirrorCS");var subQ3=sQuery(id+"F0.wireOp",EDGE,"E19.filletArc");var subQ4=sQuery(id+"F0.wireOp",EDGE,"E18.filletArc");var subQ5=sQuery(id+"F0.wireOp",EDGE,"E17.trimOffspring");var subQ6=sQuery(id+"F0.wireOp",EDGE,"E16.MirrorCS");var subQ7=sQuery(id+"F0.wireOp",EDGE,"E14.MirrorCS");var subQ8=sQuery(id+"F0.wireOp",EDGE,"E13.filletArc");var subQ9=sQuery(id+"F0.wireOp",EDGE,"E12.filletArc");var subQ10=sQuery(id+"F0.wireOp",EDGE,"E10");var subQ11=sQuery(id+"F0.wireOp",EDGE,"E9");var subQ12=sQuery(id+"F0.wireOp",EDGE,"E8.trimOffspring");var subQ13=sQuery(id+"F0.wireOp",EDGE,"E7.filletArc");var subQ14=sQuery(id+"F0.wireOp",EDGE,"E6.filletArc");var subQ15=sQuery(id+"F0.wireOp",EDGE,"E5");var subQ16=sQuery(id+"F0.wireOp",EDGE,"E4.MirrorCS");var subQ17=sQuery(id+"F0.wireOp",EDGE,"E3");var subQ18=sQuery(id+"F0.wireOp",EDGE,"E2.trimOffspring");var subQ19=sQuery(id+"F0.wireOp",EDGE,"E1");Q10=makeQuery(id+"F8.boolean.opBoolean","INTERSECT",EDGE,{"derivedFrom":[makeQuery(id+"F4.boolean.opBoolean","MERGE",FACE,{"derivedFrom":[makeQuery(id+"F2.boolean.opBoolean","MERGE",FACE,{"derivedFrom":[makeQuery(id+"F1.opExtrude","CAP_FACE",FACE,{"disambiguationData":[OSD([sQuery(id+"F0.wireOp",EDGE,"E0"),subQ19,subQ18,subQ17,subQ16,subQ15,subQ14,subQ13,subQ12,subQ11,subQ10,subQ9,subQ8,subQ7,subQ6,subQ5,subQ4,subQ3,subQ2,subQ1,subQ0])],"isStart":true}),makeQuery(id+"F2.opExtrude","CAP_FACE",FACE,{"disambiguationData":[OSD([subQ19,subQ18,subQ17,subQ16,subQ15,subQ14,subQ13,subQ12,subQ11,subQ10,subQ9,subQ8,subQ7,subQ6,subQ5,subQ4,subQ3,subQ2,subQ1,sQuery(id+"F0.wireOp",EDGE,"E22.0"),sQuery(id+"F0.wireOp",EDGE,"E22.1"),sQuery(id+"F0.wireOp",EDGE,"E22.2"),sQuery(id+"F0.wireOp",EDGE,"E22.3"),sQuery(id+"F0.wireOp",EDGE,"E22.4"),sQuery(id+"F0.wireOp",EDGE,"E22.5"),sQuery(id+"F0.wireOp",EDGE,"E22.6"),sQuery(id+"F0.wireOp",EDGE,"E22.7"),sQuery(id+"F0.wireOp",EDGE,"E22.8"),sQuery(id+"F0.wireOp",EDGE,"E22.9"),sQuery(id+"F0.wireOp",EDGE,"E22.10"),sQuery(id+"F0.wireOp",EDGE,"E22.11"),sQuery(id+"F0.wireOp",EDGE,"E22.12"),sQuery(id+"F0.wireOp",EDGE,"E22.13"),sQuery(id+"F0.wireOp",EDGE,"E22.14"),sQuery(id+"F0.wireOp",EDGE,"E22.15"),subQ0,sQuery(id+"F0.wireOp",EDGE,"E24"),sQuery(id+"F0.wireOp",EDGE,"E25.MirrorCS")])],"isStart":true})]}),makeQuery(id+"F4.opExtrude","CAP_FACE",FACE,{"disambiguationData":[OSD([sQuery(id+"F3.wireOp",EDGE,"E26.bottom"),sQuery(id+"F3.wireOp",EDGE,"E26.top"),sQuery(id+"F3.wireOp",EDGE,"E26.left"),sQuery(id+"F3.wireOp",EDGE,"E26.right"),sQuery(id+"F3.wireOp",EDGE,"E27.filletArc"),sQuery(id+"F3.wireOp",EDGE,"E28.filletArc"),sQuery(id+"F3.wireOp",EDGE,"E29.filletArc"),sQuery(id+"F3.wireOp",EDGE,"E30.filletArc")])],"isStart":true})]}),makeQuery(id+"F8.opExtrude","SWEPT_FACE",FACE,{"disambiguationData":[OSD([sQuery(id+"F6.wireOp",EDGE,"E35.0")])]})]});}
            var Q11;
            {var subQ0=sQuery(id+"F0.wireOp",EDGE,"E23.filletArc");var subQ1=sQuery(id+"F0.wireOp",EDGE,"E21.MirrorCS");var subQ2=sQuery(id+"F0.wireOp",EDGE,"E20.MirrorCS");var subQ3=sQuery(id+"F0.wireOp",EDGE,"E19.filletArc");var subQ4=sQuery(id+"F0.wireOp",EDGE,"E18.filletArc");var subQ5=sQuery(id+"F0.wireOp",EDGE,"E17.trimOffspring");var subQ6=sQuery(id+"F0.wireOp",EDGE,"E16.MirrorCS");var subQ7=sQuery(id+"F0.wireOp",EDGE,"E14.MirrorCS");var subQ8=sQuery(id+"F0.wireOp",EDGE,"E13.filletArc");var subQ9=sQuery(id+"F0.wireOp",EDGE,"E12.filletArc");var subQ10=sQuery(id+"F0.wireOp",EDGE,"E10");var subQ11=sQuery(id+"F0.wireOp",EDGE,"E9");var subQ12=sQuery(id+"F0.wireOp",EDGE,"E8.trimOffspring");var subQ13=sQuery(id+"F0.wireOp",EDGE,"E7.filletArc");var subQ14=sQuery(id+"F0.wireOp",EDGE,"E6.filletArc");var subQ15=sQuery(id+"F0.wireOp",EDGE,"E5");var subQ16=sQuery(id+"F0.wireOp",EDGE,"E4.MirrorCS");var subQ17=sQuery(id+"F0.wireOp",EDGE,"E3");var subQ18=sQuery(id+"F0.wireOp",EDGE,"E2.trimOffspring");var subQ19=sQuery(id+"F0.wireOp",EDGE,"E1");Q11=makeQuery(id+"F8.boolean.opBoolean","INTERSECT",EDGE,{"derivedFrom":[makeQuery(id+"F4.boolean.opBoolean","MERGE",FACE,{"derivedFrom":[makeQuery(id+"F2.boolean.opBoolean","MERGE",FACE,{"derivedFrom":[makeQuery(id+"F1.opExtrude","CAP_FACE",FACE,{"disambiguationData":[OSD([sQuery(id+"F0.wireOp",EDGE,"E0"),subQ19,subQ18,subQ17,subQ16,subQ15,subQ14,subQ13,subQ12,subQ11,subQ10,subQ9,subQ8,subQ7,subQ6,subQ5,subQ4,subQ3,subQ2,subQ1,subQ0])],"isStart":true}),makeQuery(id+"F2.opExtrude","CAP_FACE",FACE,{"disambiguationData":[OSD([subQ19,subQ18,subQ17,subQ16,subQ15,subQ14,subQ13,subQ12,subQ11,subQ10,subQ9,subQ8,subQ7,subQ6,subQ5,subQ4,subQ3,subQ2,subQ1,sQuery(id+"F0.wireOp",EDGE,"E22.0"),sQuery(id+"F0.wireOp",EDGE,"E22.1"),sQuery(id+"F0.wireOp",EDGE,"E22.2"),sQuery(id+"F0.wireOp",EDGE,"E22.3"),sQuery(id+"F0.wireOp",EDGE,"E22.4"),sQuery(id+"F0.wireOp",EDGE,"E22.5"),sQuery(id+"F0.wireOp",EDGE,"E22.6"),sQuery(id+"F0.wireOp",EDGE,"E22.7"),sQuery(id+"F0.wireOp",EDGE,"E22.8"),sQuery(id+"F0.wireOp",EDGE,"E22.9"),sQuery(id+"F0.wireOp",EDGE,"E22.10"),sQuery(id+"F0.wireOp",EDGE,"E22.11"),sQuery(id+"F0.wireOp",EDGE,"E22.12"),sQuery(id+"F0.wireOp",EDGE,"E22.13"),sQuery(id+"F0.wireOp",EDGE,"E22.14"),sQuery(id+"F0.wireOp",EDGE,"E22.15"),subQ0,sQuery(id+"F0.wireOp",EDGE,"E24"),sQuery(id+"F0.wireOp",EDGE,"E25.MirrorCS")])],"isStart":true})]}),makeQuery(id+"F4.opExtrude","CAP_FACE",FACE,{"disambiguationData":[OSD([sQuery(id+"F3.wireOp",EDGE,"E26.bottom"),sQuery(id+"F3.wireOp",EDGE,"E26.top"),sQuery(id+"F3.wireOp",EDGE,"E26.left"),sQuery(id+"F3.wireOp",EDGE,"E26.right"),sQuery(id+"F3.wireOp",EDGE,"E27.filletArc"),sQuery(id+"F3.wireOp",EDGE,"E28.filletArc"),sQuery(id+"F3.wireOp",EDGE,"E29.filletArc"),sQuery(id+"F3.wireOp",EDGE,"E30.filletArc")])],"isStart":true})]}),makeQuery(id+"F8.opExtrude","SWEPT_FACE",FACE,{"disambiguationData":[OSD([sQuery(id+"F6.wireOp",EDGE,"E37.trimOffspring")])]})]});}
            fillet(context, id + "F18", {"entities" : qUnion([Q0, Q1, Q2, Q3, Q4, Q5, Q6, Q7, Q8, Q9, Q10, Q11]), "radius" : 2 * mm, "tangentPropagation" : true, "allowEdgeOverflow" : false});
        }
        {
            var Q0;
            Q0=makeQuery(id+"F17.opExtrude","SWEPT_FACE",FACE,{"disambiguationData":[OSD([sQuery(id+"F3.wireOp",EDGE,"E32.1")])]});
            var sketch = newSketch(context, id + "F19", { "sketchPlane" : qUnion([Q0])});
            skArc(sketch, "E72", {"start": v(-1.14, 20.82) * mm, "mid": v(-0.04, 19.55) * mm, "end": v(1.15, 20.73) * mm});
            skLineSegment(sketch, "E73", {"start": v(1.15, 20.73) * mm, "end": v(1.15, 24) * mm});
            skLineSegment(sketch, "E74", {"start": v(-1.14, 20.82) * mm, "end": v(-1.14, 24) * mm});
            skSolve(sketch);
        }
        {
            var Q0;
            Q0=makeQuery(id+"F19.imprint","IMPRINT",FACE,{"disambiguationData":[TD([[makeQuery(id+"F19.imprint","IMPRINT",EDGE,{"derivedFrom":sQuery(id+"F19.wireOp",EDGE,"E72")}),1.0]])]});
            extrude(context, id + "F20", {"entities" : qUnion([Q0]), "operationType" : NewBodyOperationType.REMOVE, "oppositeDirection" : true, "depth" : 11 * mm, "offsetDistance" : 25 * mm});
        }
        {
            var Q0;
            Q0=makeQuery(id+"F20.boolean.opBoolean","INTERSECT",EDGE,{"derivedFrom":[makeQuery(id+"F15.opExtrude","SWEPT_FACE",FACE,{"disambiguationData":[OSD([sQuery(id+"F11.wireOp",EDGE,"E65.right")])]}),makeQuery(id+"F20.opExtrude","CAP_FACE",FACE,{"disambiguationData":[OSD([sQuery(id+"F3.wireOp",EDGE,"E32.1"),sQuery(id+"F19.wireOp",EDGE,"E72"),sQuery(id+"F19.wireOp",EDGE,"E73"),sQuery(id+"F19.wireOp",EDGE,"E74")])],"isStart":false})]});
            var Q1;
            Q1=makeQuery(id+"F20.boolean.opBoolean","INTERSECT",EDGE,{"derivedFrom":[makeQuery(id+"F15.opExtrude","SWEPT_FACE",FACE,{"disambiguationData":[OSD([sQuery(id+"F11.wireOp",EDGE,"E65.right")])]}),makeQuery(id+"F20.opExtrude","SWEPT_FACE",FACE,{"disambiguationData":[OSD([sQuery(id+"F19.wireOp",EDGE,"E72")])]})]});
            fillet(context, id + "F21", {"entities" : qUnion([Q0, Q1]), "radius" : 5 * mm, "tangentPropagation" : true, "allowEdgeOverflow" : false});
        }
        {
            var Q0;
            Q0=makeQuery(id+"F6.imprint","IMPRINT",FACE,{"disambiguationData":[TD([[makeQuery(id+"F6.imprint","IMPRINT",EDGE,{"derivedFrom":sQuery(id+"F6.wireOp",EDGE,"E44")}),1.0]])]});
            extrude(context, id + "F22", {"entities" : qUnion([Q0]), "operationType" : NewBodyOperationType.ADD, "depth" : 8 * mm, "offsetDistance" : 25 * mm});
        }
        {
            var Q0;
            Q0=qCreatedBy(makeId("Top.planeOp"),FACE);
            var sketch = newSketch(context, id + "F23", { "sketchPlane" : qUnion([Q0])});
            skLineSegment(sketch, "E75.bottom", {"start": v(23.58, 44.9) * mm, "end": v(27.18, 44.9) * mm});
            skLineSegment(sketch, "E75.top", {"start": v(23.58, 37.7) * mm, "end": v(27.18, 37.7) * mm});
            skLineSegment(sketch, "E75.left", {"start": v(23.58, 44.9) * mm, "end": v(23.58, 37.7) * mm, "construction": true});
            skLineSegment(sketch, "E75.right", {"start": v(27.18, 44.9) * mm, "end": v(27.18, 37.7) * mm});
            skLineSegment(sketch, "E76.MirrorCS", {"start": v(23.58, 44.9) * mm, "end": v(19.98, 44.9) * mm});
            skLineSegment(sketch, "E77.MirrorCS", {"start": v(23.58, 37.7) * mm, "end": v(19.98, 37.7) * mm});
            skLineSegment(sketch, "E78.MirrorCS", {"start": v(19.98, 44.9) * mm, "end": v(19.98, 37.7) * mm});
            skCircle(sketch, "E79", {"center": v(23.58, 41.3) * mm, "radius": 1.5 * mm});
            skLineSegment(sketch, "E80.0", {"start": v(23.2, 45.9) * mm, "end": v(18.98, 45.9) * mm});
            skLineSegment(sketch, "E80.1", {"start": v(28.18, 45.9) * mm, "end": v(28.18, 36.7) * mm});
            skLineSegment(sketch, "E80.2", {"start": v(23.2, 36.7) * mm, "end": v(28.18, 36.7) * mm});
            skLineSegment(sketch, "E80.3", {"start": v(23.2, 45.9) * mm, "end": v(28.18, 45.9) * mm});
            skLineSegment(sketch, "E80.4", {"start": v(23.2, 36.7) * mm, "end": v(18.98, 36.7) * mm});
            skLineSegment(sketch, "E80.5", {"start": v(18.98, 45.9) * mm, "end": v(18.98, 36.7) * mm});
            skSolve(sketch);
        }
        {
            var Q0;
            Q0=makeQuery(id+"F23.imprint","IMPRINT",FACE,{"disambiguationData":[TD([[makeQuery(id+"F23.imprint","IMPRINT",EDGE,{"derivedFrom":sQuery(id+"F23.wireOp",EDGE,"E79")}),1.0]])]});
            extrude(context, id + "F24", {"entities" : qUnion([Q0]), "operationType" : NewBodyOperationType.REMOVE, "depth" : 25 * mm, "offsetDistance" : 25 * mm});
        }
        {
            var Q0;
            Q0=makeQuery(id+"F23.imprint","IMPRINT",FACE,{"disambiguationData":[TD([[makeQuery(id+"F23.imprint","IMPRINT",EDGE,{"derivedFrom":sQuery(id+"F23.wireOp",EDGE,"E75.bottom")}),1.0]])]});
            extrude(context, id + "F25", {"entities" : qUnion([Q0]), "operationType" : NewBodyOperationType.ADD, "depth" : 5.3 * mm, "offsetDistance" : 25 * mm});
        }
        {
            var Q0;
            Q0=makeQuery(id+"F17.opExtrude","CAP_FACE",FACE,{"disambiguationData":[OSD([sQuery(id+"F3.wireOp",EDGE,"E31.0"),sQuery(id+"F3.wireOp",EDGE,"E31.1"),sQuery(id+"F3.wireOp",EDGE,"E31.2"),sQuery(id+"F3.wireOp",EDGE,"E31.3"),sQuery(id+"F3.wireOp",EDGE,"E31.4"),sQuery(id+"F3.wireOp",EDGE,"E31.5"),sQuery(id+"F3.wireOp",EDGE,"E31.6"),sQuery(id+"F3.wireOp",EDGE,"E31.7"),sQuery(id+"F3.wireOp",EDGE,"E32.0"),sQuery(id+"F3.wireOp",EDGE,"E32.1"),sQuery(id+"F3.wireOp",EDGE,"E32.2"),sQuery(id+"F3.wireOp",EDGE,"E32.3"),sQuery(id+"F3.wireOp",EDGE,"E32.4"),sQuery(id+"F3.wireOp",EDGE,"E32.5"),sQuery(id+"F3.wireOp",EDGE,"E32.6"),sQuery(id+"F3.wireOp",EDGE,"E32.7")])],"isStart":false});
            var sketch = newSketch(context, id + "F26", { "sketchPlane" : qUnion([Q0])});
            skLineSegment(sketch, "E81", {"start": v(-30.26, 68.3) * mm, "end": v(-1.15, 68.3) * mm});
            skLineSegment(sketch, "E82", {"start": v(-1.15, 68.3) * mm, "end": v(-1.15, 69.3) * mm});
            skLineSegment(sketch, "E83", {"start": v(-1.15, 69.3) * mm, "end": v(1.14, 69.3) * mm});
            skLineSegment(sketch, "E84", {"start": v(1.14, 69.3) * mm, "end": v(1.14, 68.3) * mm});
            skLineSegment(sketch, "E85", {"start": v(1.14, 68.3) * mm, "end": v(32, 68.3) * mm});
            skLineSegment(sketch, "E86", {"start": v(34, 66.3) * mm, "end": v(34, -5.79) * mm});
            skLineSegment(sketch, "E87", {"start": v(32, -7.79) * mm, "end": v(-32, -7.79) * mm});
            skLineSegment(sketch, "E88", {"start": v(-34, -5.79) * mm, "end": v(-34, 66.3) * mm});
            skLineSegment(sketch, "E89", {"start": v(-32, 68.3) * mm, "end": v(-30.26, 68.3) * mm});
            skArc(sketch, "E90.filletArc", {"start": v(34, 66.3) * mm, "mid": v(33.41, 67.71) * mm, "end": v(32, 68.3) * mm});
            skArc(sketch, "E91.filletArc", {"start": v(-32, 68.3) * mm, "mid": v(-33.41, 67.71) * mm, "end": v(-34, 66.3) * mm});
            skArc(sketch, "E92.filletArc", {"start": v(-34, -5.79) * mm, "mid": v(-33.41, -7.2) * mm, "end": v(-32, -7.79) * mm});
            skArc(sketch, "E93.filletArc", {"start": v(32, -7.79) * mm, "mid": v(33.41, -7.2) * mm, "end": v(34, -5.79) * mm});
            skCircle(sketch, "E94", {"center": v(5, 55.7) * mm, "radius": 2.77 * mm});
            skSolve(sketch);
        }
        {
            var Q0;
            Q0=makeQuery(id+"F26.imprint","IMPRINT",FACE,{"disambiguationData":[TD([[makeQuery(id+"F26.imprint","IMPRINT",EDGE,{"derivedFrom":sQuery(id+"F26.wireOp",EDGE,"E81")}),-1.0]])]});
            extrude(context, id + "F27", {"entities" : qUnion([Q0]), "depth" : 5 * mm, "offsetDistance" : 25 * mm, "hasSecondDirection" : true, "secondDirectionOppositeDirection" : false, "secondDirectionDepth" : 3 * mm});
        }
        {
            var Q0;
            Q0=makeQuery(id+"F27.opExtrude","CAP_FACE",FACE,{"disambiguationData":[OSD([sQuery(id+"F26.wireOp",EDGE,"E81"),sQuery(id+"F26.wireOp",EDGE,"E82"),sQuery(id+"F26.wireOp",EDGE,"E83"),sQuery(id+"F26.wireOp",EDGE,"E84"),sQuery(id+"F26.wireOp",EDGE,"E85"),sQuery(id+"F26.wireOp",EDGE,"E86"),sQuery(id+"F26.wireOp",EDGE,"E87"),sQuery(id+"F26.wireOp",EDGE,"E88"),sQuery(id+"F26.wireOp",EDGE,"E89"),sQuery(id+"F26.wireOp",EDGE,"E90.filletArc"),sQuery(id+"F26.wireOp",EDGE,"E91.filletArc"),sQuery(id+"F26.wireOp",EDGE,"E92.filletArc"),sQuery(id+"F26.wireOp",EDGE,"E93.filletArc"),sQuery(id+"F26.wireOp",EDGE,"E94")])],"isStart":true});
            fillet(context, id + "F28", {"entities" : qUnion([Q0]), "radius" : 0.4 * mm, "tangentPropagation" : true, "allowEdgeOverflow" : false});
        }
    });
